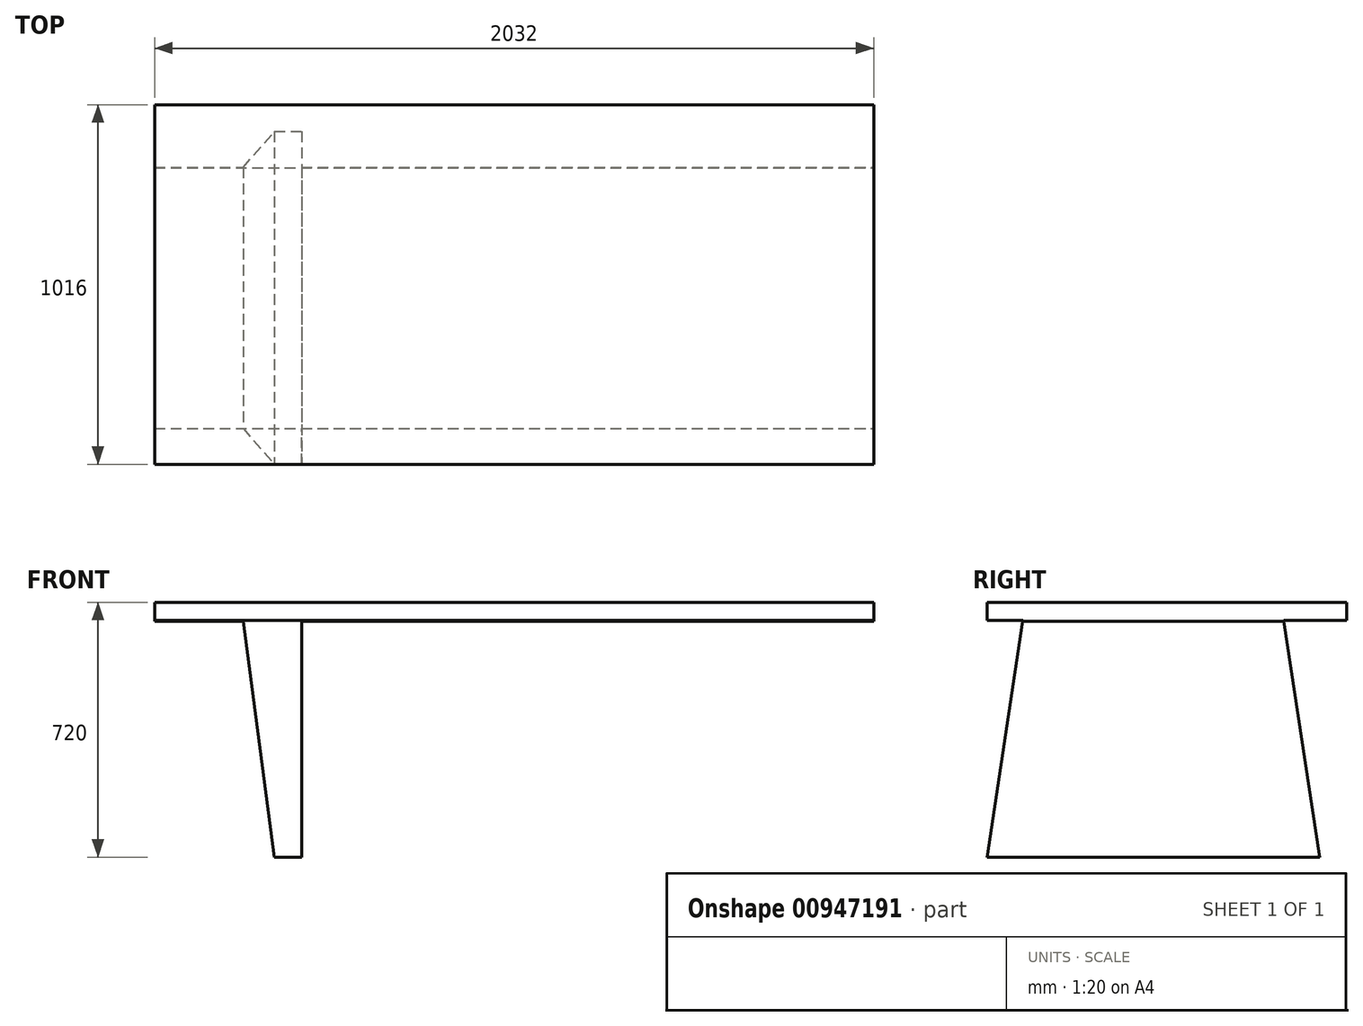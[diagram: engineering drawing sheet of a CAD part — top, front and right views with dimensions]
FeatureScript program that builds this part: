
annotation { "Feature Type Name" : "Feature", "Feature Type Description" : "" }
export const myFeature = defineFeature(function(context is Context, id is Id, definition is map)
    precondition{}
    {
        {
            var Q0;
            Q0=qCreatedBy(makeId("Top.planeOp"),FACE);
            var sketch = newSketch(context, id + "F0", { "sketchPlane" : qUnion([Q0])});
            skLineSegment(sketch, "E0.bottom", {"start": v(0, 0) * mm, "end": v(2032, 0) * mm});
            skLineSegment(sketch, "E0.top", {"start": v(0, 1016) * mm, "end": v(2032, 1016) * mm});
            skLineSegment(sketch, "E0.left", {"start": v(0, 0) * mm, "end": v(0, 1016) * mm});
            skLineSegment(sketch, "E0.right", {"start": v(2032, 0) * mm, "end": v(2032, 1016) * mm});
            skSolve(sketch);
        }
        {
            var Q0;
            Q0 = qSketchRegion(id + "F0", true);
            extrude(context, id + "F1", {"entities" : qUnion([Q0]), "depth" : 720 * mm, "offsetDistance" : 25.4 * mm});
        }
        {
            var Q0;
            Q0=makeQuery(id+"F1.opExtrude","SWEPT_FACE",FACE,{"disambiguationData":[OSD([sQuery(id+"F0.wireOp",EDGE,"E0.right")])]});
            var sketch = newSketch(context, id + "F2", { "sketchPlane" : qUnion([Q0])});
            skLineSegment(sketch, "E1.bottom", {"start": v(0, 720) * mm, "end": v(1016, 720) * mm});
            skLineSegment(sketch, "E1.top", {"start": v(0, 0) * mm, "end": v(1016, 0) * mm});
            skLineSegment(sketch, "E1.left", {"start": v(0, 720) * mm, "end": v(0, 0) * mm});
            skLineSegment(sketch, "E1.right", {"start": v(1016, 720) * mm, "end": v(1016, 0) * mm});
            skLineSegment(sketch, "E2", {"start": v(0, 669.2) * mm, "end": v(1016, 669.2) * mm});
            skLineSegment(sketch, "E3", {"start": v(1016, 0) * mm, "end": v(914.4, 669.2) * mm});
            skLineSegment(sketch, "E4", {"start": v(1016, 0) * mm, "end": v(924.74, 0) * mm});
            skLineSegment(sketch, "E5", {"start": v(940.27, 0) * mm, "end": v(838.2, 669.2) * mm});
            skLineSegment(sketch, "E6", {"start": v(0, 0) * mm, "end": v(101.6, 0) * mm});
            skLineSegment(sketch, "E7", {"start": v(76.19, 0) * mm, "end": v(76.2, 0.07) * mm});
            skLineSegment(sketch, "E8", {"start": v(0, 0) * mm, "end": v(101.6, 669.2) * mm});
            skPoint(sketch, "E9.orphan", {"position": v(939.8, 3.1) * mm});
            skPoint(sketch, "E10.orphan", {"position": v(177.8, 669.2) * mm});
            skLineSegment(sketch, "E11", {"start": v(76.2, 0.07) * mm, "end": v(177.8, 669.2) * mm});
            skLineSegment(sketch, "E12.bottom", {"start": v(1016, 720) * mm, "end": v(0, 720) * mm});
            skLineSegment(sketch, "E12.top", {"start": v(1016, 669.2) * mm, "end": v(0, 669.2) * mm});
            skLineSegment(sketch, "E12.left", {"start": v(1016, 720) * mm, "end": v(1016, 669.2) * mm});
            skLineSegment(sketch, "E12.right", {"start": v(0, 720) * mm, "end": v(0, 669.2) * mm});
            skSolve(sketch);
        }
        {
            var Q0;
            {var subQ1=sQuery(id+"F2.wireOp",EDGE,"E1.top");Q0=makeQuery(id+"F2.imprint","IMPRINT",FACE,{"disambiguationData":[TD([[makeQuery(id+"F2.imprint","IMPRINT",EDGE,{"derivedFrom":subQ1}),1.0]])]});}
            var Q1;
            {var subQ0=sQuery(id+"F2.wireOp",EDGE,"E1.left");Q1=makeQuery(id+"F2.imprint","IMPRINT",FACE,{"disambiguationData":[TD([[makeQuery(id+"F2.imprint","IMPRINT",EDGE,{"derivedFrom":subQ0}),1.0]])]});}
            var Q2;
            {var subQ0=sQuery(id+"F2.wireOp",EDGE,"E1.right");Q2=makeQuery(id+"F2.imprint","IMPRINT",FACE,{"disambiguationData":[TD([[makeQuery(id+"F2.imprint","IMPRINT",EDGE,{"derivedFrom":subQ0}),-1.0]])]});}
            extrude(context, id + "F3", {"entities" : qUnion([Q0, Q1, Q2]), "operationType" : NewBodyOperationType.REMOVE, "oppositeDirection" : true, "depth" : 3810 * mm, "offsetDistance" : 25.4 * mm});
        }
        {
            var Q0;
            Q0=qCreatedBy(makeId("Front.planeOp"),FACE);
            var sketch = newSketch(context, id + "F4", { "sketchPlane" : qUnion([Q0])});
            skLineSegment(sketch, "E13.bottom", {"start": v(3000.08, 729.92) * mm, "end": v(0, 729.92) * mm});
            skLineSegment(sketch, "E13.top", {"start": v(3000.08, 0) * mm, "end": v(0, 0) * mm});
            skLineSegment(sketch, "E13.left", {"start": v(3000.08, 729.92) * mm, "end": v(3000.08, 0) * mm});
            skLineSegment(sketch, "E13.right", {"start": v(0, 729.92) * mm, "end": v(0, 0) * mm});
            skLineSegment(sketch, "E14.top", {"start": v(3000.08, 666.42) * mm, "end": v(2750.08, 666.42) * mm});
            skLineSegment(sketch, "E14.left", {"start": v(3000.08, 729.92) * mm, "end": v(3000.08, 666.42) * mm});
            skLineSegment(sketch, "E14.right", {"start": v(0, 729.92) * mm, "end": v(0, 666.42) * mm});
            skLineSegment(sketch, "E15", {"start": v(2584.98, 666.42) * mm, "end": v(2584.98, 0) * mm});
            skLineSegment(sketch, "E16", {"start": v(2584.98, 0) * mm, "end": v(2740.59, 0) * mm});
            skLineSegment(sketch, "E17", {"start": v(2661.18, 0) * mm, "end": v(2750.08, 666.42) * mm});
            skLineSegment(sketch, "E18", {"start": v(415.1, 666.42) * mm, "end": v(415.1, 0) * mm});
            skLineSegment(sketch, "E19", {"start": v(338.9, 0) * mm, "end": v(250, 666.42) * mm});
            skLineSegment(sketch, "E20.trimOffspring", {"start": v(2584.98, 666.42) * mm, "end": v(415.1, 666.42) * mm});
            skLineSegment(sketch, "E21.trimOffspring", {"start": v(250, 666.42) * mm, "end": v(0, 666.42) * mm});
            skSolve(sketch);
        }
        {
            var Q0;
            {var subQ0=sQuery(id+"F4.wireOp",EDGE,"E15");Q0=makeQuery(id+"F4.imprint","IMPRINT",FACE,{"disambiguationData":[TD([[makeQuery(id+"F4.imprint","IMPRINT",EDGE,{"derivedFrom":subQ0}),-1.0]])]});}
            var Q1;
            {var subQ0=sQuery(id+"F4.wireOp",EDGE,"E19");Q1=makeQuery(id+"F4.imprint","IMPRINT",FACE,{"disambiguationData":[TD([[makeQuery(id+"F4.imprint","IMPRINT",EDGE,{"derivedFrom":subQ0}),1.0]])]});}
            var Q2;
            {var subQ0=sQuery(id+"F4.wireOp",EDGE,"E14.top");Q2=makeQuery(id+"F4.imprint","IMPRINT",FACE,{"disambiguationData":[TD([[makeQuery(id+"F4.imprint","IMPRINT",EDGE,{"derivedFrom":subQ0}),1.0]])]});}
            extrude(context, id + "F5", {"entities" : qUnion([Q0, Q1, Q2]), "operationType" : NewBodyOperationType.REMOVE, "oppositeDirection" : true, "depth" : 1143 * mm, "offsetDistance" : 25.4 * mm});
        }
    });
